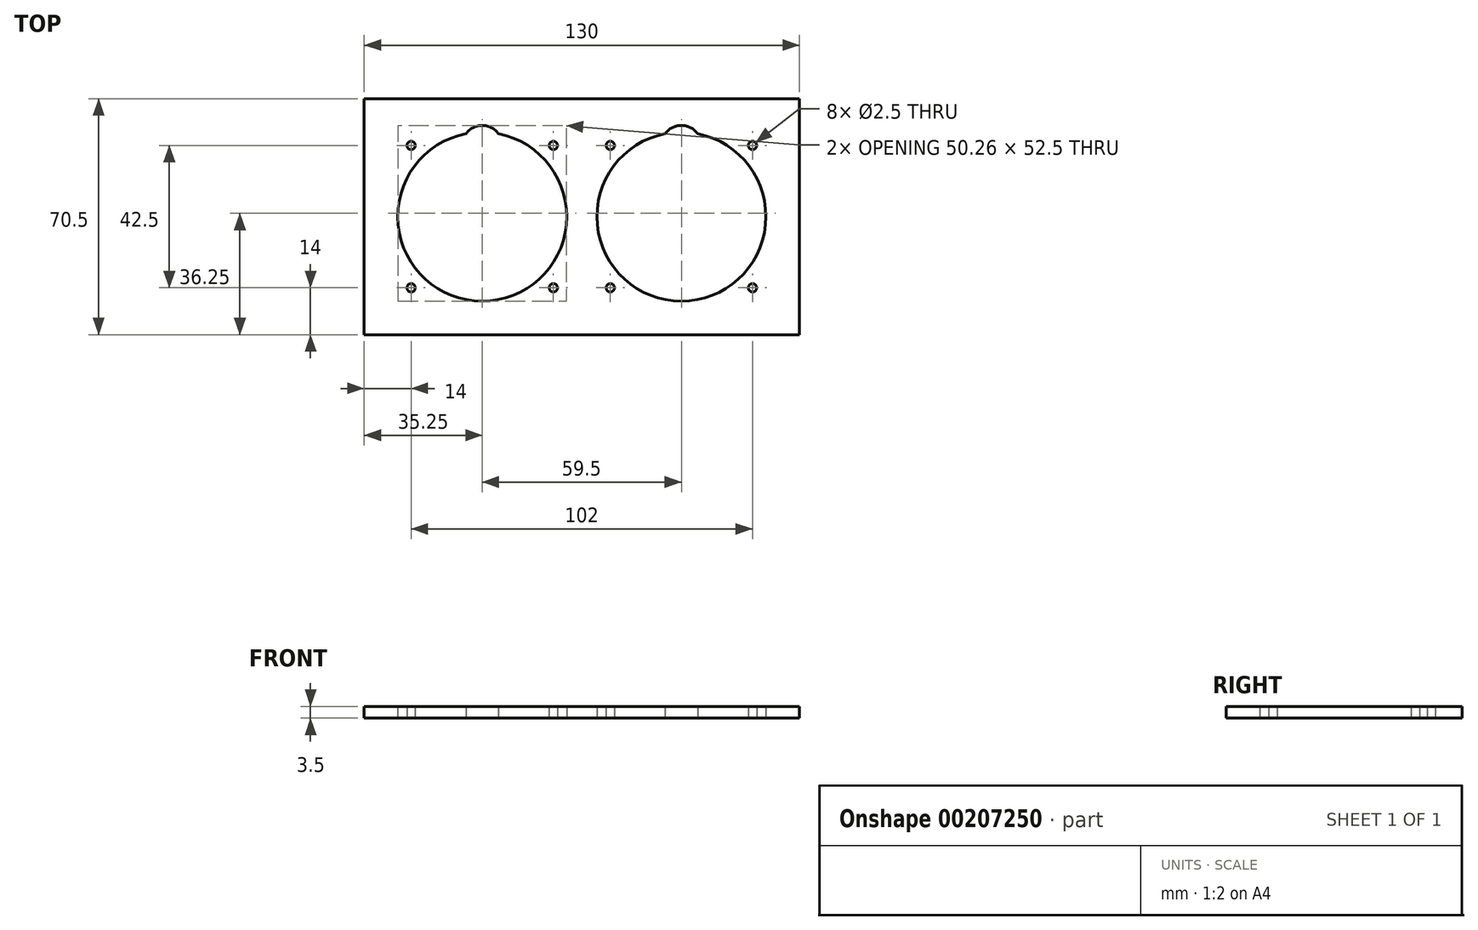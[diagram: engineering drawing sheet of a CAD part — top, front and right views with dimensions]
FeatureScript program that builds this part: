
annotation { "Feature Type Name" : "Feature", "Feature Type Description" : "" }
export const myFeature = defineFeature(function(context is Context, id is Id, definition is map)
    precondition{}
    {
        {
            var Q0;
            Q0=qCreatedBy(makeId("Top.planeOp"),FACE);
            var sketch = newSketch(context, id + "F0", { "sketchPlane" : qUnion([Q0])});
            skLineSegment(sketch, "E0", {"start": v(-29.75, 0) * mm, "end": v(0, 0) * mm, "construction": true});
            skLineSegment(sketch, "E1", {"start": v(29.75, 0) * mm, "end": v(0, 0) * mm, "construction": true});
            skLineSegment(sketch, "E2", {"start": v(-51, 21.25) * mm, "end": v(64.22, 21.25) * mm, "construction": true});
            skLineSegment(sketch, "E3", {"start": v(65.43, -21.25) * mm, "end": v(-51, -21.25) * mm, "construction": true});
            skLineSegment(sketch, "E4", {"start": v(-8.5, 39.08) * mm, "end": v(-8.5, -29.75) * mm, "construction": true});
            skLineSegment(sketch, "E5", {"start": v(-51, 34.84) * mm, "end": v(-51, -29.75) * mm, "construction": true});
            skLineSegment(sketch, "E6.bottom", {"start": v(-65, -35.25) * mm, "end": v(65, -35.25) * mm});
            skLineSegment(sketch, "E6.top", {"start": v(-65, 35.25) * mm, "end": v(65, 35.25) * mm});
            skLineSegment(sketch, "E6.left", {"start": v(-65, -35.25) * mm, "end": v(-65, 35.25) * mm});
            skLineSegment(sketch, "E6.right", {"start": v(65, -35.25) * mm, "end": v(65, 35.25) * mm});
            skLineSegment(sketch, "E7", {"start": v(0, 39.29) * mm, "end": v(0, -35.25) * mm, "construction": true});
            skPoint(sketch, "E8", {"position": v(-51, 21.25) * mm});
            skPoint(sketch, "E9", {"position": v(-8.5, 21.25) * mm});
            skPoint(sketch, "E10", {"position": v(-8.5, -21.25) * mm});
            skPoint(sketch, "E11", {"position": v(-51, -21.25) * mm});
            skPoint(sketch, "E12.MirrorP", {"position": v(8.5, 21.25) * mm});
            skPoint(sketch, "E13.MirrorP", {"position": v(51, 21.25) * mm});
            skPoint(sketch, "E14.MirrorP", {"position": v(51, -21.25) * mm});
            skPoint(sketch, "E15.MirrorP", {"position": v(8.5, -21.25) * mm});
            skLineSegment(sketch, "E16", {"start": v(-65, 35.25) * mm, "end": v(-65, 44.03) * mm, "construction": true});
            skLineSegment(sketch, "E17", {"start": v(-65, 40.48) * mm, "end": v(0, 40.48) * mm, "construction": true});
            skLineSegment(sketch, "E18", {"start": v(65, 40.48) * mm, "end": v(0, 40.48) * mm, "construction": true});
            skPoint(sketch, "E19.center", {"position": v(-29.75, 0) * mm});
            skPoint(sketch, "E20.center", {"position": v(29.75, 0) * mm});
            skCircle(sketch, "E21", {"center": v(-29.75, 0) * mm, "radius": 1.5 * mm});
            skCircle(sketch, "E22.MirrorC", {"center": v(29.75, 0) * mm, "radius": 1.5 * mm});
            skArc(sketch, "E23", {"start": v(-34.6, 24.78) * mm, "mid": v(-29.75, -25.25) * mm, "end": v(-24.9, 24.78) * mm});
            skArc(sketch, "E24", {"start": v(24.9, 24.78) * mm, "mid": v(29.75, -25.25) * mm, "end": v(34.6, 24.78) * mm});
            skArc(sketch, "E25", {"start": v(-24.9, 24.78) * mm, "mid": v(-29.75, 27.25) * mm, "end": v(-34.6, 24.78) * mm});
            skArc(sketch, "E26", {"start": v(34.6, 24.78) * mm, "mid": v(29.75, 27.25) * mm, "end": v(24.9, 24.78) * mm});
            skLineSegment(sketch, "E27.bottom", {"start": v(0, 29.75) * mm, "end": v(-59.5, 29.75) * mm, "construction": true});
            skLineSegment(sketch, "E27.top", {"start": v(0, -29.75) * mm, "end": v(-59.5, -29.75) * mm, "construction": true});
            skLineSegment(sketch, "E27.left", {"start": v(0, 29.75) * mm, "end": v(0, -29.75) * mm});
            skLineSegment(sketch, "E27.right", {"start": v(-59.5, 29.75) * mm, "end": v(-59.5, -29.75) * mm, "construction": true});
            skSolve(sketch);
        }
        {
            var Q0;
            Q0=makeQuery(id+"F0.imprint","IMPRINT",FACE,{"disambiguationData":[TD([[makeQuery(id+"F0.imprint","IMPRINT",EDGE,{"derivedFrom":sQuery(id+"F0.wireOp",EDGE,"0BlL0anx-IE55-3Ffi-SPci-i4BzROD0rsbx")}),-1.0]])]});
            var Q1;
            {var subQ3=sQuery(id+"F0.wireOp",EDGE,"E6.bottom");Q1=makeQuery(id+"F0.imprint","IMPRINT",FACE,{"disambiguationData":[TD([[makeQuery(id+"F0.imprint","IMPRINT",EDGE,{"derivedFrom":subQ3}),1.0]])]});}
            extrude(context, id + "F1", {"entities" : qUnion([Q0, Q1]), "depth" : 3.5 * mm});
        }
        {
            var Q0;
            Q0=sQuery(id+"F0.wireOp",VERTEX,"E8");
            var Q1;
            Q1=sQuery(id+"F0.wireOp",VERTEX,"E11");
            var Q2;
            Q2=sQuery(id+"F0.wireOp",VERTEX,"E10");
            var Q3;
            Q3=sQuery(id+"F0.wireOp",VERTEX,"E9");
            var Q4;
            Q4=sQuery(id+"F0.wireOp",VERTEX,"E12.MirrorP");
            var Q5;
            Q5=sQuery(id+"F0.wireOp",VERTEX,"E15.MirrorP");
            var Q6;
            Q6=sQuery(id+"F0.wireOp",VERTEX,"E14.MirrorP");
            var Q7;
            Q7=sQuery(id+"F0.wireOp",VERTEX,"E13.MirrorP");
            var Q8;
            Q8=makeQuery(id+"F1.opExtrude","SWEPT_BODY",BODY,{"disambiguationData":[OSD([sQuery(id+"F0.wireOp",EDGE,"0BlL0anx-IE55-3Ffi-SPci-i4BzROD0rsbx"),sQuery(id+"F0.wireOp",EDGE,"11NtaD0y-CNwM-gsSJ-spU2-3III16kJOtdG"),sQuery(id+"F0.wireOp",EDGE,"E6.bottom"),sQuery(id+"F0.wireOp",EDGE,"E6.top"),sQuery(id+"F0.wireOp",EDGE,"E6.left"),sQuery(id+"F0.wireOp",EDGE,"E6.right")])]});
            hole(context, id + "F2", {"style" : HoleStyle.SIMPLE, "endStyle" : HoleEndStyle.THROUGH, "oppositeDirection" : true, "holeDiameter" : 2.5 * mm, "startFromSketch" : true, "locations" : qUnion([Q0, Q1, Q2, Q3, Q4, Q5, Q6, Q7]), "scope" : qUnion([Q8]), "isTappedThrough" : true});
        }
    });
